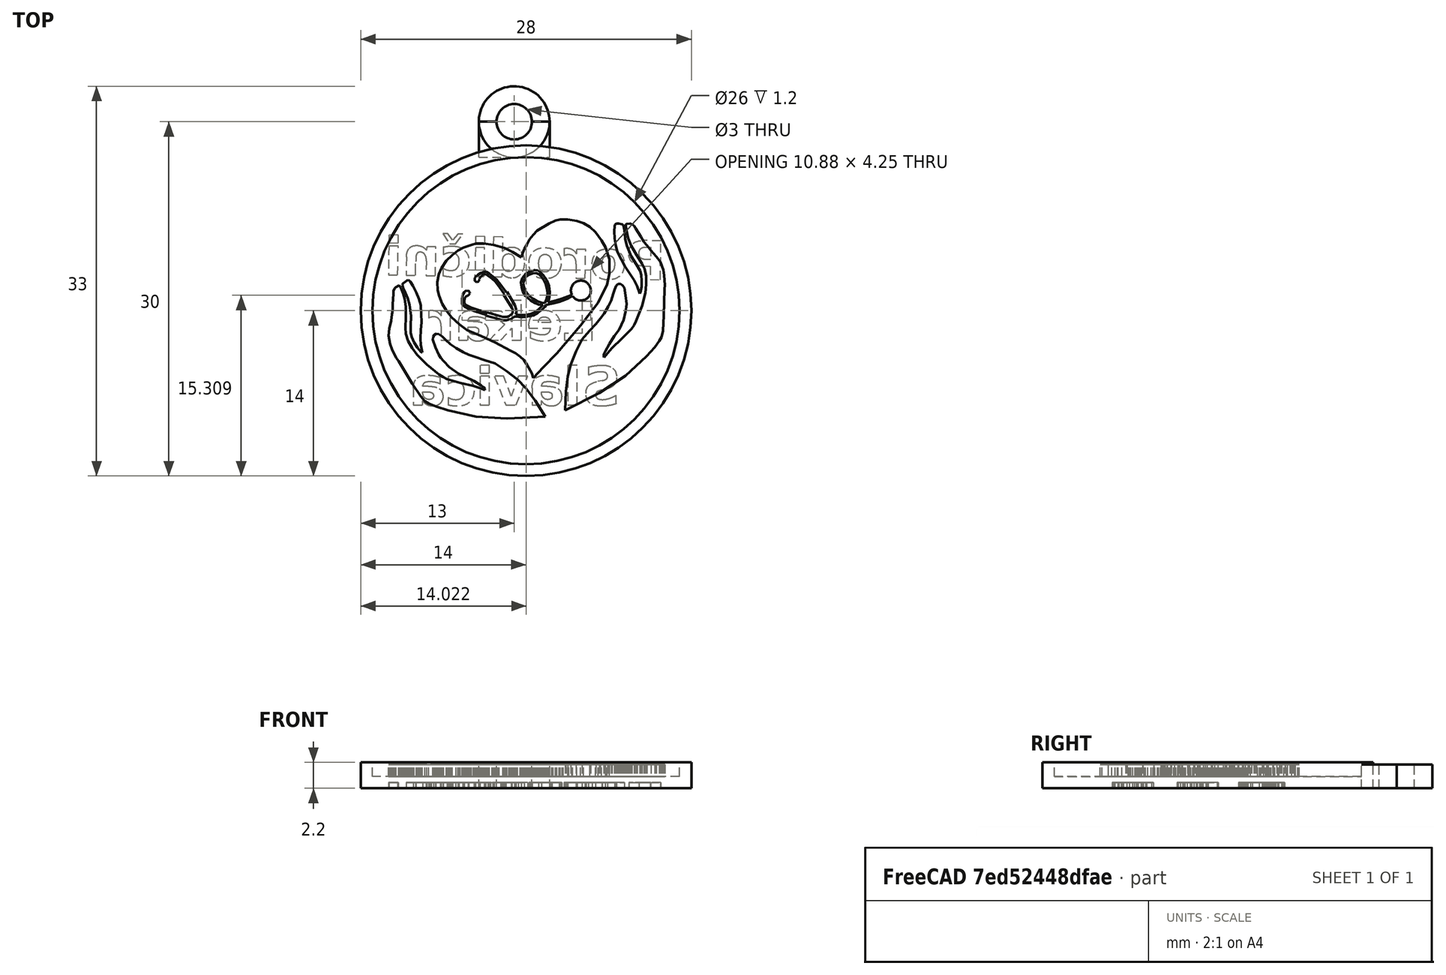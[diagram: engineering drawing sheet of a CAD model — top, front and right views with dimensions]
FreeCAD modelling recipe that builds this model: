
FCSTD DOCUMENT  (FreeCAD 0.19R)
Label: PLS_logo
License: All rights reserved
LicenseURL: http://en.wikipedia.org/wiki/All_rights_reserved
objects: Part::Extrusion×7, Part::Cut×7, Sketcher::SketchObject×4, PartDesign::Body×4, Part::Cylinder×4, Part::Part2DObjectPython×3, Part::Box×1
note: 30 computed .brp shape members not serialized (recipe doc carries the construction recipe); baked Part::Feature solids carry a one-line shape summary decoded from their .brp

FEATURE [Sketcher::SketchObject] Sketch
  MapMode = 5
  Support = -> [XY_Plane]
  sketch-geometry (100):
    g0: LineSegment StartX=-7.99466 StartY=7.65686 StartZ=0 EndX=-8.31629 EndY=7.67321 EndZ=0
    g1: LineSegment StartX=-8.31629 StartY=7.67321 StartZ=0 EndX=-8.46348 EndY=7.62415 EndZ=0
    g2: LineSegment StartX=-8.46348 StartY=7.62415 StartZ=0 EndX=-8.64882 EndY=7.49332 EndZ=0
    g3: LineSegment StartX=-8.64882 StartY=7.49332 StartZ=0 EndX=-8.78511 EndY=7.26436 EndZ=0
    g4: LineSegment StartX=-8.78511 StartY=7.26436 StartZ=0 EndX=-9.23757 EndY=6.56114 EndZ=0
    g5: LineSegment StartX=-9.23757 StartY=6.56114 StartZ=0 EndX=-9.49378 EndY=6.12503 EndZ=0
    g6: LineSegment StartX=-9.49378 StartY=6.12503 StartZ=0 EndX=-9.72819 EndY=5.84156 EndZ=0
    g7: LineSegment StartX=-9.72819 StartY=5.84156 StartZ=0 EndX=-10.0771 EndY=5.40545 EndZ=0
    g8: LineSegment StartX=-10.0771 StartY=5.40545 StartZ=0 EndX=-10.5241 EndY=4.89848 EndZ=0
    g9: LineSegment StartX=-10.5241 StartY=4.89848 StartZ=0 EndX=-10.8784 EndY=4.42966 EndZ=0
    g10: LineSegment StartX=-10.8784 StartY=4.42966 StartZ=0 EndX=-11.1183 EndY=3.7537 EndZ=0
    g11: LineSegment StartX=-11.1183 StartY=3.7537 StartZ=0 EndX=-11.2099 EndY=3.2849 EndZ=0
    g12: LineSegment StartX=-11.2099 StartY=3.2849 StartZ=0 EndX=-11.2683 EndY=2.47003 EndZ=0
    g13: LineSegment StartX=-11.2683 StartY=2.47003 StartZ=0 EndX=-11.2318 EndY=2.13385 EndZ=0
    g14: LineSegment StartX=-11.2318 StartY=2.13385 StartZ=0 EndX=-11.1697 EndY=-0.093535 EndZ=0
    g15: LineSegment StartX=-11.1697 StartY=-0.093535 StartZ=0 EndX=-11.099 EndY=-1.41517 EndZ=0
    g16: LineSegment StartX=-11.099 StartY=-1.41517 StartZ=0 EndX=-10.9851 EndY=-1.92752 EndZ=0
    g17: LineSegment StartX=-10.9851 StartY=-1.92752 StartZ=0 EndX=-10.7981 EndY=-2.25282 EndZ=0
    g18: LineSegment StartX=-10.7981 StartY=-2.25282 StartZ=0 EndX=-10.4077 EndY=-2.78956 EndZ=0
    g19: LineSegment StartX=-10.4077 StartY=-2.78956 StartZ=0 EndX=-9.69294 EndY=-3.55814 EndZ=0
    g20: LineSegment StartX=-9.69294 StartY=-3.55814 StartZ=0 EndX=-7.92061 EndY=-5.20964 EndZ=0
    g21: LineSegment StartX=-7.92061 StartY=-5.20964 StartZ=0 EndX=-5.70519 EndY=-6.65973 EndZ=0
    g22: LineSegment StartX=-5.70519 StartY=-6.65973 StartZ=0 EndX=-2.80501 EndY=-8.1501 EndZ=0
    g23: LineSegment StartX=-2.80501 StartY=-8.1501 StartZ=0 EndX=-2.88557 EndY=-6.53889 EndZ=0
    g24: LineSegment StartX=-2.88557 StartY=-6.53889 StartZ=0 EndX=-3.04596 EndY=-5.2378 EndZ=0
    g25: LineSegment StartX=-3.04596 StartY=-5.2378 StartZ=0 EndX=-3.28765 EndY=-4.27108 EndZ=0
    g26: LineSegment StartX=-3.28765 StartY=-4.27108 StartZ=0 EndX=-3.73073 EndY=-3.14323 EndZ=0
    g27: LineSegment StartX=-3.73073 StartY=-3.14323 StartZ=0 EndX=-4.25437 EndY=-2.13622 EndZ=0
    g28: LineSegment StartX=-4.25437 StartY=-2.13622 StartZ=0 EndX=-4.89343 EndY=-1.4123 EndZ=0
    g29: LineSegment StartX=-4.89343 StartY=-1.4123 StartZ=0 EndX=-5.42724 EndY=-0.829955 EndZ=0
    g30: LineSegment StartX=-5.42724 StartY=-0.829955 StartZ=0 EndX=-5.80334 EndY=-0.368932 EndZ=0
    g31: LineSegment StartX=-5.80334 StartY=-0.368932 StartZ=0 EndX=-6.11862 EndY=0.058717 EndZ=0
    g32: LineSegment StartX=-6.11862 StartY=0.058717 StartZ=0 EndX=-6.47672 EndY=0.661651 EndZ=0
    g33: LineSegment StartX=-6.47672 StartY=0.661651 StartZ=0 EndX=-6.71059 EndY=1.16227 EndZ=0
    g34: LineSegment StartX=-6.71059 StartY=1.16227 StartZ=0 EndX=-6.86944 EndY=1.70125 EndZ=0
    g35: LineSegment StartX=-6.86944 StartY=1.70125 StartZ=0 EndX=-6.99076 EndY=2.10161 EndZ=0
    g36: LineSegment StartX=-6.99076 StartY=2.10161 StartZ=0 EndX=-7.14848 EndY=2.40492 EndZ=0
    g37: LineSegment StartX=-7.14848 StartY=2.40492 StartZ=0 EndX=-7.30619 EndY=2.5505 EndZ=0
    g38: LineSegment StartX=-7.30619 StartY=2.5505 StartZ=0 EndX=-7.51244 EndY=2.5505 EndZ=0
    g39: LineSegment StartX=-7.51244 StartY=2.5505 StartZ=0 EndX=-7.67016 EndY=2.44131 EndZ=0
    g40: LineSegment StartX=-7.67016 StartY=2.44131 StartZ=0 EndX=-7.82788 EndY=2.2472 EndZ=0
    g41: LineSegment StartX=-7.82788 StartY=2.2472 StartZ=0 EndX=-7.93707 EndY=1.59206 EndZ=0
    g42: LineSegment StartX=-7.93707 StartY=1.59206 StartZ=0 EndX=-8.00986 EndY=0.87626 EndZ=0
    g43: LineSegment StartX=-8.00986 StartY=0.87626 StartZ=0 EndX=-7.99773 EndY=0.585087 EndZ=0
    g44: LineSegment StartX=-7.99773 StartY=0.585087 StartZ=0 EndX=-7.92494 EndY=0.221122 EndZ=0
    g45: LineSegment StartX=-7.92494 StartY=0.221122 StartZ=0 EndX=-7.75509 EndY=-0.470414 EndZ=0
    g46: LineSegment StartX=-7.75509 StartY=-0.470414 StartZ=0 EndX=-7.37899 EndY=-1.2954 EndZ=0
    g47: LineSegment StartX=-7.37899 StartY=-1.2954 StartZ=0 EndX=-6.97863 EndY=-1.85348 EndZ=0
    g48: LineSegment StartX=-6.97863 StartY=-1.85348 StartZ=0 EndX=-6.554 EndY=-2.52075 EndZ=0
    g49: LineSegment StartX=-6.554 StartY=-2.52075 StartZ=0 EndX=-6.20216 EndY=-3.16376 EndZ=0
    g50: LineSegment StartX=-6.20216 StartY=-3.16376 StartZ=0 EndX=-6.09298 EndY=-3.41854 EndZ=0
    g51: LineSegment StartX=-6.09298 StartY=-3.41854 StartZ=0 EndX=-6.09298 EndY=-3.57626 EndZ=0
    g52: LineSegment StartX=-6.09298 StartY=-3.57626 StartZ=0 EndX=-6.12937 EndY=-3.66118 EndZ=0
    g53: LineSegment StartX=-6.12937 StartY=-3.66118 StartZ=0 EndX=-6.39628 EndY=-3.32148 EndZ=0
    g54: LineSegment StartX=-6.39628 StartY=-3.32148 StartZ=0 EndX=-6.79664 EndY=-2.84832 EndZ=0
    g55: LineSegment StartX=-6.79664 StartY=-2.84832 StartZ=0 EndX=-7.62163 EndY=-2.07186 EndZ=0
    g56: LineSegment StartX=-7.62163 StartY=-2.07186 StartZ=0 EndX=-8.43449 EndY=-1.24687 EndZ=0
    g57: LineSegment StartX=-8.43449 StartY=-1.24687 StartZ=0 EndX=-8.65287 EndY=-0.919304 EndZ=0
    g58: LineSegment StartX=-8.65287 StartY=-0.919304 StartZ=0 EndX=-8.81059 EndY=-0.579603 EndZ=0
    g59: LineSegment StartX=-8.81059 StartY=-0.579603 StartZ=0 EndX=-9.31856 EndY=0.683537 EndZ=0
    g60: LineSegment StartX=-9.31856 StartY=0.683537 StartZ=0 EndX=-9.60815 EndY=1.80568 EndZ=0
    g61: LineSegment StartX=-9.60815 StartY=1.80568 StartZ=0 EndX=-9.68054 EndY=2.52965 EndZ=0
    g62: LineSegment StartX=-9.68054 StartY=2.52965 StartZ=0 EndX=-9.68054 EndY=3.21741 EndZ=0
    g63: LineSegment StartX=-9.68054 StartY=3.21741 StartZ=0 EndX=-9.55385 EndY=3.83278 EndZ=0
    g64: LineSegment StartX=-9.55385 StartY=3.83278 StartZ=0 EndX=-9.31856 EndY=4.28526 EndZ=0
    g65: LineSegment StartX=-9.31856 StartY=4.28526 StartZ=0 EndX=-8.83633 EndY=5.03517 EndZ=0
    g66: LineSegment StartX=-8.83633 StartY=5.03517 StartZ=0 EndX=-8.40195 EndY=5.81343 EndZ=0
    g67: LineSegment StartX=-8.40195 StartY=5.81343 StartZ=0 EndX=-8.14856 EndY=6.4469 EndZ=0
    g68: LineSegment StartX=-8.14856 StartY=6.4469 StartZ=0 EndX=-8.03997 EndY=6.88128 EndZ=0
    g69: LineSegment StartX=-8.03997 StartY=6.88128 StartZ=0 EndX=-7.96757 EndY=7.38806 EndZ=0
    g70: LineSegment StartX=-7.96757 StartY=7.38806 StartZ=0 EndX=-7.96757 EndY=7.60525 EndZ=0
    g71: LineSegment StartX=-7.96757 StartY=7.60525 StartZ=0 EndX=-7.99466 EndY=7.65686 EndZ=0
    g72: LineSegment StartX=-7.37277 StartY=7.68163 StartZ=0 EndX=-7.63261 EndY=7.62489 EndZ=0
    g73: LineSegment StartX=-7.63261 StartY=7.62489 StartZ=0 EndX=-7.7302 EndY=7.55983 EndZ=0
    g74: LineSegment StartX=-7.7302 StartY=7.55983 StartZ=0 EndX=-7.79526 EndY=7.30773 EndZ=0
    g75: LineSegment StartX=-7.79526 StartY=7.30773 StartZ=0 EndX=-7.86032 EndY=6.83604 EndZ=0
    g76: LineSegment StartX=-7.86032 StartY=6.83604 StartZ=0 EndX=-7.89285 EndY=6.37249 EndZ=0
    g77: LineSegment StartX=-7.89285 StartY=6.37249 StartZ=0 EndX=-8.04736 EndY=5.78695 EndZ=0
    g78: LineSegment StartX=-8.04736 StartY=5.78695 StartZ=0 EndX=-8.41333 EndY=4.91677 EndZ=0
    g79: LineSegment StartX=-8.41333 StartY=4.91677 StartZ=0 EndX=-8.86062 EndY=4.20925 EndZ=0
    g80: LineSegment StartX=-8.86062 StartY=4.20925 StartZ=0 EndX=-9.15339 EndY=3.68877 EndZ=0
    g81: LineSegment StartX=-9.15339 StartY=3.68877 StartZ=0 EndX=-9.25098 EndY=3.32281 EndZ=0
    g82: LineSegment StartX=-9.25098 StartY=3.32281 StartZ=0 EndX=-9.3079 EndY=2.83486 EndZ=0
    g83: LineSegment StartX=-9.3079 StartY=2.83486 StartZ=0 EndX=-9.2835 EndY=2.33878 EndZ=0
    g84: LineSegment StartX=-9.2835 StartY=2.33878 StartZ=0 EndX=-9.21031 EndY=1.87522 EndZ=0
    g85: LineSegment StartX=-9.21031 StartY=1.87522 StartZ=0 EndX=-9.12899 EndY=1.7451 EndZ=0
    g86: LineSegment StartX=-9.12899 StartY=1.7451 StartZ=0 EndX=-8.91754 EndY=2.3713 EndZ=0
    g87: LineSegment StartX=-8.91754 StartY=2.3713 StartZ=0 EndX=-8.64917 EndY=2.88365 EndZ=0
    g88: LineSegment StartX=-8.64917 StartY=2.88365 StartZ=0 EndX=-8.28321 EndY=3.46919 EndZ=0
    g89: LineSegment StartX=-8.28321 StartY=3.46919 StartZ=0 EndX=-7.89285 EndY=4.0222 EndZ=0
    g90: LineSegment StartX=-7.89285 StartY=4.0222 StartZ=0 EndX=-7.57568 EndY=4.64027 EndZ=0
    g91: LineSegment StartX=-7.57568 StartY=4.64027 StartZ=0 EndX=-7.24225 EndY=5.29087 EndZ=0
    g92: LineSegment StartX=-7.24225 StartY=5.29087 StartZ=0 EndX=-7.104 EndY=5.82761 EndZ=0
    g93: LineSegment StartX=-7.104 StartY=5.82761 StartZ=0 EndX=-7.01454 EndY=6.41315 EndZ=0
    g94: LineSegment StartX=-7.01454 StartY=6.41315 StartZ=0 EndX=-6.99014 EndY=7.03935 EndZ=0
    g95: LineSegment StartX=-6.99014 StartY=7.03935 StartZ=0 EndX=-7.01454 EndY=7.44598 EndZ=0
    g96: LineSegment StartX=-7.01454 StartY=7.44598 StartZ=0 EndX=-7.0308 EndY=7.59236 EndZ=0
    g97: LineSegment StartX=-7.0308 StartY=7.59236 StartZ=0 EndX=-7.104 EndY=7.64929 EndZ=0
    g98: LineSegment StartX=-7.104 StartY=7.64929 StartZ=0 EndX=-7.20972 EndY=7.67369 EndZ=0
    g99: LineSegment StartX=-7.20972 StartY=7.67369 StartZ=0 EndX=-7.37277 EndY=7.68163 EndZ=0
  constraints (98):
    c: Coincident(g0,g1)
    c: Coincident(g1,g2)
    c: Coincident(g2,g3)
    c: Coincident(g3,g4)
    c: Coincident(g4,g5)
    c: Coincident(g5,g6)
    c: Coincident(g6,g7)
    c: Coincident(g7,g8)
    c: Coincident(g8,g9)
    c: Coincident(g9,g10)
    c: Coincident(g10,g11)
    c: Coincident(g11,g12)
    c: Coincident(g12,g13)
    c: Coincident(g13,g14)
    c: Coincident(g14,g15)
    c: Coincident(g15,g16)
    c: Coincident(g16,g17)
    c: Coincident(g17,g18)
    c: Coincident(g18,g19)
    c: Coincident(g19,g20)
    c: Coincident(g20,g21)
    c: Coincident(g21,g22)
    c: Coincident(g22,g23)
    c: Coincident(g23,g24)
    c: Coincident(g24,g25)
    c: Coincident(g25,g26)
    c: Coincident(g26,g27)
    c: Coincident(g27,g28)
    c: Coincident(g28,g29)
    c: Coincident(g29,g30)
    c: Coincident(g31,g32)
    c: Coincident(g32,g33)
    c: Coincident(g33,g34)
    c: Coincident(g34,g35)
    c: Coincident(g35,g36)
    c: Coincident(g36,g37)
    c: Coincident(g37,g38)
    c: Coincident(g38,g39)
    c: Coincident(g39,g40)
    c: Coincident(g40,g41)
    c: Coincident(g41,g42)
    c: Coincident(g42,g43)
    c: Coincident(g43,g44)
    c: Coincident(g44,g45)
    c: Coincident(g45,g46)
    c: Coincident(g46,g47)
    c: Coincident(g47,g48)
    c: Coincident(g48,g49)
    c: Coincident(g49,g50)
    c: Coincident(g50,g51)
    c: Coincident(g51,g52)
    c: Coincident(g52,g53)
    c: Coincident(g53,g54)
    c: Coincident(g54,g55)
    c: Coincident(g55,g56)
    c: Coincident(g56,g57)
    c: Coincident(g57,g58)
    c: Coincident(g58,g59)
    c: Coincident(g59,g60)
    c: Coincident(g60,g61)
    c: Coincident(g61,g62)
    c: Coincident(g62,g63)
    c: Coincident(g63,g64)
    c: Coincident(g64,g65)
    c: Coincident(g65,g66)
    c: Coincident(g66,g67)
    c: Coincident(g67,g68)
    c: Coincident(g68,g69)
    c: Coincident(g69,g70)
    c: Coincident(g0,g71)
    c: Coincident(g72,g73)
    c: Coincident(g73,g74)
    c: Coincident(g74,g75)
    c: Coincident(g75,g76)
    c: Coincident(g76,g77)
    c: Coincident(g77,g78)
    c: Coincident(g78,g79)
    c: Coincident(g79,g80)
    c: Coincident(g80,g81)
    c: Coincident(g81,g82)
    c: Coincident(g82,g83)
    c: Coincident(g83,g84)
    c: Coincident(g84,g85)
    c: Coincident(g85,g86)
    c: Coincident(g86,g87)
    c: Coincident(g87,g88)
    c: Coincident(g88,g89)
    c: Coincident(g89,g90)
    c: Coincident(g90,g91)
    c: Coincident(g91,g92)
    c: Coincident(g92,g93)
    c: Coincident(g93,g94)
    c: Coincident(g94,g95)
    c: Coincident(g95,g96)
    c: Coincident(g96,g97)
    c: Coincident(g97,g98)
    c: Coincident(g98,g99)
    c: Coincident(g99,g72)
FEATURE [PartDesign::Body] Body
  Group = -> [Sketch]
  Origin = -> Origin
FEATURE [Part::Extrusion] Extrude
  Base = -> Sketch
  Dir = (0,0,1)
  DirMode = 2
  FaceMakerClass = Part::FaceMakerBullseye
  LengthFwd = 1
  LengthRev = 0
  Placement = pos=(1,19.5,1) rot=(0,0,1;0.523599rad)
  Solid = true
  Symmetric = false
FEATURE [Sketcher::SketchObject] Sketch001
  MapMode = 5
  Support = -> [XY_Plane001]
  sketch-geometry (100):
    g0: LineSegment StartX=-7.99466 StartY=7.65686 StartZ=0 EndX=-8.31629 EndY=7.67321 EndZ=0
    g1: LineSegment StartX=-8.31629 StartY=7.67321 StartZ=0 EndX=-8.46348 EndY=7.62415 EndZ=0
    g2: LineSegment StartX=-8.46348 StartY=7.62415 StartZ=0 EndX=-8.64882 EndY=7.49332 EndZ=0
    g3: LineSegment StartX=-8.64882 StartY=7.49332 StartZ=0 EndX=-8.78511 EndY=7.26436 EndZ=0
    g4: LineSegment StartX=-8.78511 StartY=7.26436 StartZ=0 EndX=-9.23757 EndY=6.56114 EndZ=0
    g5: LineSegment StartX=-9.23757 StartY=6.56114 StartZ=0 EndX=-9.49378 EndY=6.12503 EndZ=0
    g6: LineSegment StartX=-9.49378 StartY=6.12503 StartZ=0 EndX=-9.72819 EndY=5.84156 EndZ=0
    g7: LineSegment StartX=-9.72819 StartY=5.84156 StartZ=0 EndX=-10.0771 EndY=5.40545 EndZ=0
    g8: LineSegment StartX=-10.0771 StartY=5.40545 StartZ=0 EndX=-10.5241 EndY=4.89848 EndZ=0
    g9: LineSegment StartX=-10.5241 StartY=4.89848 StartZ=0 EndX=-10.8784 EndY=4.42966 EndZ=0
    g10: LineSegment StartX=-10.8784 StartY=4.42966 StartZ=0 EndX=-11.1183 EndY=3.7537 EndZ=0
    g11: LineSegment StartX=-11.1183 StartY=3.7537 StartZ=0 EndX=-11.2099 EndY=3.2849 EndZ=0
    g12: LineSegment StartX=-11.2099 StartY=3.2849 StartZ=0 EndX=-11.2683 EndY=2.47003 EndZ=0
    g13: LineSegment StartX=-11.2683 StartY=2.47003 StartZ=0 EndX=-11.2318 EndY=2.13385 EndZ=0
    g14: LineSegment StartX=-11.2318 StartY=2.13385 StartZ=0 EndX=-11.1697 EndY=-0.093535 EndZ=0
    g15: LineSegment StartX=-11.1697 StartY=-0.093535 StartZ=0 EndX=-11.099 EndY=-1.41517 EndZ=0
    g16: LineSegment StartX=-11.099 StartY=-1.41517 StartZ=0 EndX=-10.9851 EndY=-1.92752 EndZ=0
    g17: LineSegment StartX=-10.9851 StartY=-1.92752 StartZ=0 EndX=-10.7981 EndY=-2.25282 EndZ=0
    g18: LineSegment StartX=-10.7981 StartY=-2.25282 StartZ=0 EndX=-10.4077 EndY=-2.78956 EndZ=0
    g19: LineSegment StartX=-10.4077 StartY=-2.78956 StartZ=0 EndX=-9.69294 EndY=-3.55814 EndZ=0
    g20: LineSegment StartX=-9.69294 StartY=-3.55814 StartZ=0 EndX=-7.92061 EndY=-5.20964 EndZ=0
    g21: LineSegment StartX=-7.92061 StartY=-5.20964 StartZ=0 EndX=-5.70519 EndY=-6.65973 EndZ=0
    g22: LineSegment StartX=-5.70519 StartY=-6.65973 StartZ=0 EndX=-2.80501 EndY=-8.1501 EndZ=0
    g23: LineSegment StartX=-2.80501 StartY=-8.1501 StartZ=0 EndX=-2.88557 EndY=-6.53889 EndZ=0
    g24: LineSegment StartX=-2.88557 StartY=-6.53889 StartZ=0 EndX=-3.04596 EndY=-5.2378 EndZ=0
    g25: LineSegment StartX=-3.04596 StartY=-5.2378 StartZ=0 EndX=-3.28765 EndY=-4.27108 EndZ=0
    g26: LineSegment StartX=-3.28765 StartY=-4.27108 StartZ=0 EndX=-3.73073 EndY=-3.14323 EndZ=0
    g27: LineSegment StartX=-3.73073 StartY=-3.14323 StartZ=0 EndX=-4.25437 EndY=-2.13622 EndZ=0
    g28: LineSegment StartX=-4.25437 StartY=-2.13622 StartZ=0 EndX=-4.89343 EndY=-1.4123 EndZ=0
    g29: LineSegment StartX=-4.89343 StartY=-1.4123 StartZ=0 EndX=-5.42724 EndY=-0.829955 EndZ=0
    g30: LineSegment StartX=-5.42724 StartY=-0.829955 StartZ=0 EndX=-5.80334 EndY=-0.368932 EndZ=0
    g31: LineSegment StartX=-5.80334 StartY=-0.368932 StartZ=0 EndX=-6.11862 EndY=0.058717 EndZ=0
    g32: LineSegment StartX=-6.11862 StartY=0.058717 StartZ=0 EndX=-6.47672 EndY=0.661651 EndZ=0
    g33: LineSegment StartX=-6.47672 StartY=0.661651 StartZ=0 EndX=-6.71059 EndY=1.16227 EndZ=0
    g34: LineSegment StartX=-6.71059 StartY=1.16227 StartZ=0 EndX=-6.86944 EndY=1.70125 EndZ=0
    g35: LineSegment StartX=-6.86944 StartY=1.70125 StartZ=0 EndX=-6.99076 EndY=2.10161 EndZ=0
    g36: LineSegment StartX=-6.99076 StartY=2.10161 StartZ=0 EndX=-7.14848 EndY=2.40492 EndZ=0
    g37: LineSegment StartX=-7.14848 StartY=2.40492 StartZ=0 EndX=-7.30619 EndY=2.5505 EndZ=0
    g38: LineSegment StartX=-7.30619 StartY=2.5505 StartZ=0 EndX=-7.51244 EndY=2.5505 EndZ=0
    g39: LineSegment StartX=-7.51244 StartY=2.5505 StartZ=0 EndX=-7.67016 EndY=2.44131 EndZ=0
    g40: LineSegment StartX=-7.67016 StartY=2.44131 StartZ=0 EndX=-7.82788 EndY=2.2472 EndZ=0
    g41: LineSegment StartX=-7.82788 StartY=2.2472 StartZ=0 EndX=-7.93707 EndY=1.59206 EndZ=0
    g42: LineSegment StartX=-7.93707 StartY=1.59206 StartZ=0 EndX=-8.00986 EndY=0.87626 EndZ=0
    g43: LineSegment StartX=-8.00986 StartY=0.87626 StartZ=0 EndX=-7.99773 EndY=0.585087 EndZ=0
    g44: LineSegment StartX=-7.99773 StartY=0.585087 StartZ=0 EndX=-7.92494 EndY=0.221122 EndZ=0
    g45: LineSegment StartX=-7.92494 StartY=0.221122 StartZ=0 EndX=-7.75509 EndY=-0.470414 EndZ=0
    g46: LineSegment StartX=-7.75509 StartY=-0.470414 StartZ=0 EndX=-7.37899 EndY=-1.2954 EndZ=0
    g47: LineSegment StartX=-7.37899 StartY=-1.2954 StartZ=0 EndX=-6.97863 EndY=-1.85348 EndZ=0
    g48: LineSegment StartX=-6.97863 StartY=-1.85348 StartZ=0 EndX=-6.554 EndY=-2.52075 EndZ=0
    g49: LineSegment StartX=-6.554 StartY=-2.52075 StartZ=0 EndX=-6.20216 EndY=-3.16376 EndZ=0
    g50: LineSegment StartX=-6.20216 StartY=-3.16376 StartZ=0 EndX=-6.09298 EndY=-3.41854 EndZ=0
    g51: LineSegment StartX=-6.09298 StartY=-3.41854 StartZ=0 EndX=-6.09298 EndY=-3.57626 EndZ=0
    g52: LineSegment StartX=-6.09298 StartY=-3.57626 StartZ=0 EndX=-6.12937 EndY=-3.66118 EndZ=0
    g53: LineSegment StartX=-6.12937 StartY=-3.66118 StartZ=0 EndX=-6.39628 EndY=-3.32148 EndZ=0
    g54: LineSegment StartX=-6.39628 StartY=-3.32148 StartZ=0 EndX=-6.79664 EndY=-2.84832 EndZ=0
    g55: LineSegment StartX=-6.79664 StartY=-2.84832 StartZ=0 EndX=-7.62163 EndY=-2.07186 EndZ=0
    g56: LineSegment StartX=-7.62163 StartY=-2.07186 StartZ=0 EndX=-8.43449 EndY=-1.24687 EndZ=0
    g57: LineSegment StartX=-8.43449 StartY=-1.24687 StartZ=0 EndX=-8.65287 EndY=-0.919304 EndZ=0
    g58: LineSegment StartX=-8.65287 StartY=-0.919304 StartZ=0 EndX=-8.81059 EndY=-0.579603 EndZ=0
    g59: LineSegment StartX=-8.81059 StartY=-0.579603 StartZ=0 EndX=-9.31856 EndY=0.683537 EndZ=0
    g60: LineSegment StartX=-9.31856 StartY=0.683537 StartZ=0 EndX=-9.60815 EndY=1.80568 EndZ=0
    g61: LineSegment StartX=-9.60815 StartY=1.80568 StartZ=0 EndX=-9.68054 EndY=2.52965 EndZ=0
    g62: LineSegment StartX=-9.68054 StartY=2.52965 StartZ=0 EndX=-9.68054 EndY=3.21741 EndZ=0
    g63: LineSegment StartX=-9.68054 StartY=3.21741 StartZ=0 EndX=-9.55385 EndY=3.83278 EndZ=0
    g64: LineSegment StartX=-9.55385 StartY=3.83278 StartZ=0 EndX=-9.31856 EndY=4.28526 EndZ=0
    g65: LineSegment StartX=-9.31856 StartY=4.28526 StartZ=0 EndX=-8.83633 EndY=5.03517 EndZ=0
    g66: LineSegment StartX=-8.83633 StartY=5.03517 StartZ=0 EndX=-8.40195 EndY=5.81343 EndZ=0
    g67: LineSegment StartX=-8.40195 StartY=5.81343 StartZ=0 EndX=-8.14856 EndY=6.4469 EndZ=0
    g68: LineSegment StartX=-8.14856 StartY=6.4469 StartZ=0 EndX=-8.03997 EndY=6.88128 EndZ=0
    g69: LineSegment StartX=-8.03997 StartY=6.88128 StartZ=0 EndX=-7.96757 EndY=7.38806 EndZ=0
    g70: LineSegment StartX=-7.96757 StartY=7.38806 StartZ=0 EndX=-7.96757 EndY=7.60525 EndZ=0
    g71: LineSegment StartX=-7.96757 StartY=7.60525 StartZ=0 EndX=-7.99466 EndY=7.65686 EndZ=0
    g72: LineSegment StartX=-7.37277 StartY=7.68163 StartZ=0 EndX=-7.63261 EndY=7.62489 EndZ=0
    g73: LineSegment StartX=-7.63261 StartY=7.62489 StartZ=0 EndX=-7.7302 EndY=7.55983 EndZ=0
    g74: LineSegment StartX=-7.7302 StartY=7.55983 StartZ=0 EndX=-7.79526 EndY=7.30773 EndZ=0
    g75: LineSegment StartX=-7.79526 StartY=7.30773 StartZ=0 EndX=-7.86032 EndY=6.83604 EndZ=0
    g76: LineSegment StartX=-7.86032 StartY=6.83604 StartZ=0 EndX=-7.89285 EndY=6.37249 EndZ=0
    g77: LineSegment StartX=-7.89285 StartY=6.37249 StartZ=0 EndX=-8.04736 EndY=5.78695 EndZ=0
    g78: LineSegment StartX=-8.04736 StartY=5.78695 StartZ=0 EndX=-8.41333 EndY=4.91677 EndZ=0
    g79: LineSegment StartX=-8.41333 StartY=4.91677 StartZ=0 EndX=-8.86062 EndY=4.20925 EndZ=0
    g80: LineSegment StartX=-8.86062 StartY=4.20925 StartZ=0 EndX=-9.15339 EndY=3.68877 EndZ=0
    g81: LineSegment StartX=-9.15339 StartY=3.68877 StartZ=0 EndX=-9.25098 EndY=3.32281 EndZ=0
    g82: LineSegment StartX=-9.25098 StartY=3.32281 StartZ=0 EndX=-9.3079 EndY=2.83486 EndZ=0
    g83: LineSegment StartX=-9.3079 StartY=2.83486 StartZ=0 EndX=-9.2835 EndY=2.33878 EndZ=0
    g84: LineSegment StartX=-9.2835 StartY=2.33878 StartZ=0 EndX=-9.21031 EndY=1.87522 EndZ=0
    g85: LineSegment StartX=-9.21031 StartY=1.87522 StartZ=0 EndX=-9.12899 EndY=1.7451 EndZ=0
    g86: LineSegment StartX=-9.12899 StartY=1.7451 StartZ=0 EndX=-8.91754 EndY=2.3713 EndZ=0
    g87: LineSegment StartX=-8.91754 StartY=2.3713 StartZ=0 EndX=-8.64917 EndY=2.88365 EndZ=0
    g88: LineSegment StartX=-8.64917 StartY=2.88365 StartZ=0 EndX=-8.28321 EndY=3.46919 EndZ=0
    g89: LineSegment StartX=-8.28321 StartY=3.46919 StartZ=0 EndX=-7.89285 EndY=4.0222 EndZ=0
    g90: LineSegment StartX=-7.89285 StartY=4.0222 StartZ=0 EndX=-7.57568 EndY=4.64027 EndZ=0
    g91: LineSegment StartX=-7.57568 StartY=4.64027 StartZ=0 EndX=-7.24225 EndY=5.29087 EndZ=0
    g92: LineSegment StartX=-7.24225 StartY=5.29087 StartZ=0 EndX=-7.104 EndY=5.82761 EndZ=0
    g93: LineSegment StartX=-7.104 StartY=5.82761 StartZ=0 EndX=-7.01454 EndY=6.41315 EndZ=0
    g94: LineSegment StartX=-7.01454 StartY=6.41315 StartZ=0 EndX=-6.99014 EndY=7.03935 EndZ=0
    g95: LineSegment StartX=-6.99014 StartY=7.03935 StartZ=0 EndX=-7.01454 EndY=7.44598 EndZ=0
    g96: LineSegment StartX=-7.01454 StartY=7.44598 StartZ=0 EndX=-7.0308 EndY=7.59236 EndZ=0
    g97: LineSegment StartX=-7.0308 StartY=7.59236 StartZ=0 EndX=-7.104 EndY=7.64929 EndZ=0
    g98: LineSegment StartX=-7.104 StartY=7.64929 StartZ=0 EndX=-7.20972 EndY=7.67369 EndZ=0
    g99: LineSegment StartX=-7.20972 StartY=7.67369 StartZ=0 EndX=-7.37277 EndY=7.68163 EndZ=0
  constraints (98):
    c: Coincident(g0,g1)
    c: Coincident(g1,g2)
    c: Coincident(g2,g3)
    c: Coincident(g3,g4)
    c: Coincident(g4,g5)
    c: Coincident(g5,g6)
    c: Coincident(g6,g7)
    c: Coincident(g7,g8)
    c: Coincident(g8,g9)
    c: Coincident(g9,g10)
    c: Coincident(g10,g11)
    c: Coincident(g11,g12)
    c: Coincident(g12,g13)
    c: Coincident(g13,g14)
    c: Coincident(g14,g15)
    c: Coincident(g15,g16)
    c: Coincident(g16,g17)
    c: Coincident(g17,g18)
    c: Coincident(g18,g19)
    c: Coincident(g19,g20)
    c: Coincident(g20,g21)
    c: Coincident(g21,g22)
    c: Coincident(g22,g23)
    c: Coincident(g23,g24)
    c: Coincident(g24,g25)
    c: Coincident(g25,g26)
    c: Coincident(g26,g27)
    c: Coincident(g27,g28)
    c: Coincident(g28,g29)
    c: Coincident(g29,g30)
    c: Coincident(g31,g32)
    c: Coincident(g32,g33)
    c: Coincident(g33,g34)
    c: Coincident(g34,g35)
    c: Coincident(g35,g36)
    c: Coincident(g36,g37)
    c: Coincident(g37,g38)
    c: Coincident(g38,g39)
    c: Coincident(g39,g40)
    c: Coincident(g40,g41)
    c: Coincident(g41,g42)
    c: Coincident(g42,g43)
    c: Coincident(g43,g44)
    c: Coincident(g44,g45)
    c: Coincident(g45,g46)
    c: Coincident(g46,g47)
    c: Coincident(g47,g48)
    c: Coincident(g48,g49)
    c: Coincident(g49,g50)
    c: Coincident(g50,g51)
    c: Coincident(g51,g52)
    c: Coincident(g52,g53)
    c: Coincident(g53,g54)
    c: Coincident(g54,g55)
    c: Coincident(g55,g56)
    c: Coincident(g56,g57)
    c: Coincident(g57,g58)
    c: Coincident(g58,g59)
    c: Coincident(g59,g60)
    c: Coincident(g60,g61)
    c: Coincident(g61,g62)
    c: Coincident(g62,g63)
    c: Coincident(g63,g64)
    c: Coincident(g64,g65)
    c: Coincident(g65,g66)
    c: Coincident(g66,g67)
    c: Coincident(g67,g68)
    c: Coincident(g68,g69)
    c: Coincident(g69,g70)
    c: Coincident(g0,g71)
    c: Coincident(g72,g73)
    c: Coincident(g73,g74)
    c: Coincident(g74,g75)
    c: Coincident(g75,g76)
    c: Coincident(g76,g77)
    c: Coincident(g77,g78)
    c: Coincident(g78,g79)
    c: Coincident(g79,g80)
    c: Coincident(g80,g81)
    c: Coincident(g81,g82)
    c: Coincident(g82,g83)
    c: Coincident(g83,g84)
    c: Coincident(g84,g85)
    c: Coincident(g85,g86)
    c: Coincident(g86,g87)
    c: Coincident(g87,g88)
    c: Coincident(g88,g89)
    c: Coincident(g89,g90)
    c: Coincident(g90,g91)
    c: Coincident(g91,g92)
    c: Coincident(g92,g93)
    c: Coincident(g93,g94)
    c: Coincident(g94,g95)
    c: Coincident(g95,g96)
    c: Coincident(g96,g97)
    c: Coincident(g97,g98)
    c: Coincident(g98,g99)
    c: Coincident(g99,g72)
FEATURE [Sketcher::SketchObject] Sketch002
  MapMode = 5
  Support = -> [XY_Plane002]
  sketch-geometry (53):
    g0: LineSegment StartX=-1.58869 StartY=8.51607 StartZ=0 EndX=-2.26809 EndY=8.62526 EndZ=0
    g1: LineSegment StartX=-2.26809 StartY=8.62526 StartZ=0 EndX=-2.8019 EndY=8.64952 EndZ=0
    g2: LineSegment StartX=-2.8019 StartY=8.64952 StartZ=0 EndX=-3.42064 EndY=8.57673 EndZ=0
    g3: LineSegment StartX=-3.42064 StartY=8.57673 StartZ=0 EndX=-4.10005 EndY=8.40688 EndZ=0
    g4: LineSegment StartX=-4.10005 StartY=8.40688 StartZ=0 EndX=-4.76732 EndY=8.07931 EndZ=0
    g5: LineSegment StartX=-4.76732 StartY=8.07931 StartZ=0 EndX=-5.21621 EndY=7.73961 EndZ=0
    g6: LineSegment StartX=-5.21621 StartY=7.73961 StartZ=0 EndX=-5.65297 EndY=7.21793 EndZ=0
    g7: LineSegment StartX=-5.65297 StartY=7.21793 StartZ=0 EndX=-5.98054 EndY=6.59919 EndZ=0
    g8: LineSegment StartX=-5.98054 StartY=6.59919 StartZ=0 EndX=-6.11399 EndY=6.1139 EndZ=0
    g9: LineSegment StartX=-6.11399 StartY=6.1139 StartZ=0 EndX=-6.23531 EndY=5.41023 EndZ=0
    g10: LineSegment StartX=-6.23531 StartY=5.41023 StartZ=0 EndX=-6.19892 EndY=4.75509 EndZ=0
    g11: LineSegment StartX=-6.19892 StartY=4.75509 StartZ=0 EndX=-6.11399 EndY=4.05143 EndZ=0
    g12: LineSegment StartX=-6.11399 StartY=4.05143 StartZ=0 EndX=-5.82282 EndY=3.19004 EndZ=0
    g13: LineSegment StartX=-5.82282 StartY=3.19004 StartZ=0 EndX=-5.50738 EndY=2.43785 EndZ=0
    g14: LineSegment StartX=-5.50738 StartY=2.43785 StartZ=0 EndX=-4.73092 EndY=1.40661 EndZ=0
    g15: LineSegment StartX=-4.73092 StartY=1.40661 StartZ=0 EndX=-3.98305 EndY=0.340156 EndZ=0
    g16: LineSegment StartX=-3.98305 StartY=0.340156 StartZ=0 EndX=-3.20233 EndY=-0.904109 EndZ=0
    g17: LineSegment StartX=-3.20233 StartY=-0.904109 StartZ=0 EndX=-2.93268 EndY=-1.32413 EndZ=0
    g18: LineSegment StartX=-2.93268 StartY=-1.32413 StartZ=0 EndX=-2.72553 EndY=-1.75479 EndZ=0
    g19: LineSegment StartX=-2.72553 StartY=-1.75479 StartZ=0 EndX=-2.62195 EndY=-2.16364 EndZ=0
    g20: LineSegment StartX=-2.62195 StartY=-2.16364 StartZ=0 EndX=-2.57289 EndY=-2.70332 EndZ=0
    g21: LineSegment StartX=-2.57289 StartY=-2.70332 StartZ=0 EndX=-2.58924 EndY=-3.4556 EndZ=0
    g22: LineSegment StartX=-2.58924 StartY=-3.4556 StartZ=0 EndX=-2.67102 EndY=-3.87536 EndZ=0
    g23: LineSegment StartX=-2.67102 StartY=-3.87536 StartZ=0 EndX=-1.48262 EndY=-3.51557 EndZ=0
    g24: LineSegment StartX=-1.48262 StartY=-3.51557 StartZ=0 EndX=0.092815 EndY=-3.06311 EndZ=0
    g25: LineSegment StartX=0.092815 StartY=-3.06311 StartZ=0 EndX=3.01261 EndY=-2.045 EndZ=0
    g26: LineSegment StartX=3.01261 StartY=-2.045 StartZ=0 EndX=5.275 EndY=-1.10385 EndZ=0
    g27: LineSegment StartX=5.275 StartY=-1.10385 StartZ=0 EndX=6.70483 EndY=-0.144598 EndZ=0
    g28: LineSegment StartX=6.70483 StartY=-0.144598 StartZ=0 EndX=7.33829 EndY=0.561267 EndZ=0
    g29: LineSegment StartX=7.33829 StartY=0.561267 StartZ=0 EndX=7.93557 EndY=1.61102 EndZ=0
    g30: LineSegment StartX=7.93557 StartY=1.61102 StartZ=0 EndX=8.14627 EndY=2.62316 EndZ=0
    g31: LineSegment StartX=8.14627 StartY=2.62316 StartZ=0 EndX=8.13814 EndY=3.32255 EndZ=0
    g32: LineSegment StartX=8.13814 StartY=3.32255 StartZ=0 EndX=8.06495 EndY=4.17646 EndZ=0
    g33: LineSegment StartX=8.06495 StartY=4.17646 StartZ=0 EndX=7.86519 EndY=4.81764 EndZ=0
    g34: LineSegment StartX=7.86519 StartY=4.81764 StartZ=0 EndX=7.57402 EndY=5.35146 EndZ=0
    g35: LineSegment StartX=7.57402 StartY=5.35146 StartZ=0 EndX=7.16153 EndY=5.81248 EndZ=0
    g36: LineSegment StartX=7.16153 StartY=5.81248 StartZ=0 EndX=6.55492 EndY=6.29777 EndZ=0
    g37: LineSegment StartX=6.55492 StartY=6.29777 StartZ=0 EndX=6.01286 EndY=6.59157 EndZ=0
    g38: LineSegment StartX=6.01286 StartY=6.59157 StartZ=0 EndX=5.60624 EndY=6.72982 EndZ=0
    g39: LineSegment StartX=5.60624 StartY=6.72982 StartZ=0 EndX=4.99631 EndY=6.77049 EndZ=0
    g40: LineSegment StartX=4.99631 StartY=6.77049 StartZ=0 EndX=3.83336 EndY=6.76235 EndZ=0
    g41: LineSegment StartX=3.83336 StartY=6.76235 StartZ=0 EndX=3.37795 EndY=6.63223 EndZ=0
    g42: LineSegment StartX=3.37795 StartY=6.63223 StartZ=0 EndX=2.92253 EndY=6.43705 EndZ=0
    g43: LineSegment StartX=2.92253 StartY=6.43705 StartZ=0 EndX=2.48338 EndY=6.17682 EndZ=0
    g44: LineSegment StartX=2.48338 StartY=6.17682 StartZ=0 EndX=2.11741 EndY=5.94097 EndZ=0
    g45: LineSegment StartX=2.11741 StartY=5.94097 StartZ=0 EndX=1.83278 EndY=5.7458 EndZ=0
    g46: LineSegment StartX=1.83278 StartY=5.7458 StartZ=0 EndX=1.54001 EndY=5.47743 EndZ=0
    g47: LineSegment StartX=1.54001 StartY=5.47743 StartZ=0 EndX=1.14965 EndY=6.21748 EndZ=0
    g48: LineSegment StartX=1.14965 StartY=6.21748 StartZ=0 EndX=0.686102 EndY=6.87621 EndZ=0
    g49: LineSegment StartX=0.686102 StartY=6.87621 StartZ=0 EndX=0.04516 EndY=7.55052 EndZ=0
    g50: LineSegment StartX=0.04516 StartY=7.55052 StartZ=0 EndX=-0.646099 EndY=8.0954 EndZ=0
    g51: LineSegment StartX=-0.646099 StartY=8.0954 StartZ=0 EndX=-1.15844 EndY=8.3963 EndZ=0
    g52: LineSegment StartX=-1.15844 StartY=8.3963 StartZ=0 EndX=-1.58869 EndY=8.51607 EndZ=0
  constraints (52):
    c: Coincident(g0,g1)
    c: Coincident(g1,g2)
    c: Coincident(g2,g3)
    c: Coincident(g3,g4)
    c: Coincident(g4,g5)
    c: Coincident(g5,g6)
    c: Coincident(g6,g7)
    c: Coincident(g7,g8)
    c: Coincident(g8,g9)
    c: Coincident(g9,g10)
    c: Coincident(g10,g11)
    c: Coincident(g11,g12)
    c: Coincident(g12,g13)
    c: Coincident(g13,g14)
    c: Coincident(g14,g15)
    c: Coincident(g15,g16)
    c: Coincident(g16,g17)
    c: Coincident(g17,g18)
    c: Coincident(g18,g19)
    c: Coincident(g19,g20)
    c: Coincident(g20,g21)
    c: Coincident(g21,g22)
    c: Coincident(g22,g23)
    c: Coincident(g23,g24)
    c: Coincident(g24,g25)
    c: Coincident(g25,g26)
    c: Coincident(g26,g27)
    c: Coincident(g27,g28)
    c: Coincident(g28,g29)
    c: Coincident(g29,g30)
    c: Coincident(g30,g31)
    c: Coincident(g31,g32)
    c: Coincident(g33,g34)
    c: Coincident(g34,g35)
    c: Coincident(g35,g36)
    c: Coincident(g36,g37)
    c: Coincident(g37,g38)
    c: Coincident(g38,g39)
    c: Coincident(g39,g40)
    c: Coincident(g40,g41)
    c: Coincident(g41,g42)
    c: Coincident(g42,g43)
    c: Coincident(g43,g44)
    c: Coincident(g44,g45)
    c: Coincident(g45,g46)
    c: Coincident(g46,g47)
    c: Coincident(g47,g48)
    c: Coincident(g48,g49)
    c: Coincident(g49,g50)
    c: Coincident(g50,g51)
    c: Coincident(g51,g52)
    c: Coincident(g0,g52)
FEATURE [PartDesign::Body] Body001
  Group = -> [Sketch002]
  Origin = -> Origin001
FEATURE [Part::Extrusion] Extrude002
  Base = -> Sketch002
  Dir = (0,0,1)
  DirMode = 2
  FaceMakerClass = Part::FaceMakerBullseye
  LengthFwd = 1
  LengthRev = 0
  Placement = pos=(2,19,0) rot=(0,0,1;0.523599rad)
  Solid = true
  Symmetric = false
FEATURE [PartDesign::Body] Body002
  Origin = -> Origin002
FEATURE [Sketcher::SketchObject] Sketch003
  MapMode = 5
  Support = -> [XY_Plane004]
  sketch-geometry (147):
    g0: LineSegment StartX=-4.74287 StartY=4.61966 StartZ=0 EndX=-4.55753 EndY=4.91949 EndZ=0
    g1: LineSegment StartX=-4.55753 StartY=4.91949 StartZ=0 EndX=-4.4267 EndY=5.12119 EndZ=0
    g2: LineSegment StartX=-4.4267 StartY=5.12119 StartZ=0 EndX=-4.27406 EndY=5.26292 EndZ=0
    g3: LineSegment StartX=-4.27406 StartY=5.26292 StartZ=0 EndX=-4.11052 EndY=5.35014 EndZ=0
    g4: LineSegment StartX=-4.11052 StartY=5.35014 StartZ=0 EndX=-3.97423 EndY=5.37195 EndZ=0
    g5: LineSegment StartX=-3.97423 StartY=5.37195 StartZ=0 EndX=-3.85976 EndY=5.33924 EndZ=0
    g6: LineSegment StartX=-3.85976 StartY=5.33924 StartZ=0 EndX=-3.72892 EndY=5.22476 EndZ=0
    g7: LineSegment StartX=-3.72892 StartY=5.22476 StartZ=0 EndX=-3.70712 EndY=5.12119 EndZ=0
    g8: LineSegment StartX=-3.70712 StartY=5.12119 StartZ=0 EndX=-3.75073 EndY=5.02851 EndZ=0
    g9: LineSegment StartX=-3.75073 StartY=5.02851 StartZ=0 EndX=-3.88156 EndY=4.94674 EndZ=0
    g10: LineSegment StartX=-3.88156 StartY=4.94674 StartZ=0 EndX=-4.0233 EndY=4.93039 EndZ=0
    g11: LineSegment StartX=-4.0233 StartY=4.93039 StartZ=0 EndX=-4.11597 EndY=4.95765 EndZ=0
    g12: LineSegment StartX=-4.11597 StartY=4.95765 StartZ=0 EndX=-4.23045 EndY=4.93584 EndZ=0
    g13: LineSegment StartX=-4.23045 StartY=4.93584 StartZ=0 EndX=-4.34492 EndY=4.84317 EndZ=0
    g14: LineSegment StartX=-4.34492 StartY=4.84317 StartZ=0 EndX=-4.45395 EndY=4.72869 EndZ=0
    g15: LineSegment StartX=-4.45395 StartY=4.72869 StartZ=0 EndX=-4.53572 EndY=4.58696 EndZ=0
    g16: LineSegment StartX=-4.53572 StartY=4.58696 StartZ=0 EndX=-4.56298 EndY=4.46703 EndZ=0
    g17: LineSegment StartX=-4.56298 StartY=4.46703 StartZ=0 EndX=-4.54117 EndY=4.35255 EndZ=0
    g18: LineSegment StartX=-4.54117 StartY=4.35255 StartZ=0 EndX=-4.2702 EndY=3.93667 EndZ=0
    g19: LineSegment StartX=-4.2702 StartY=3.93667 StartZ=0 EndX=-3.31154 EndY=2.85309 EndZ=0
    g20: LineSegment StartX=-3.31154 StartY=2.85309 StartZ=0 EndX=-3.27866 EndY=2.87866 EndZ=0
    g21: LineSegment StartX=-3.27866 StartY=2.87866 StartZ=0 EndX=-2.31031 EndY=1.87743 EndZ=0
    g22: LineSegment StartX=-2.31031 StartY=1.87743 StartZ=0 EndX=-2.23357 EndY=1.82262 EndZ=0
    g23: LineSegment StartX=-2.23357 StartY=1.82262 StartZ=0 EndX=-2.13856 EndY=1.77146 EndZ=0
    g24: LineSegment StartX=-2.13856 StartY=1.77146 StartZ=0 EndX=-2.03625 EndY=1.72395 EndZ=0
    g25: LineSegment StartX=-2.03625 StartY=1.72395 StartZ=0 EndX=-1.84988 EndY=1.6801 EndZ=0
    g26: LineSegment StartX=-1.84988 StartY=1.6801 StartZ=0 EndX=-1.69641 EndY=1.69837 EndZ=0
    g27: LineSegment StartX=-1.69641 StartY=1.69837 StartZ=0 EndX=-1.53563 EndY=1.73492 EndZ=0
    g28: LineSegment StartX=-1.53563 StartY=1.73492 StartZ=0 EndX=-1.426 EndY=1.808 EndZ=0
    g29: LineSegment StartX=-1.426 StartY=1.808 StartZ=0 EndX=-1.34927 EndY=1.92859 EndZ=0
    g30: LineSegment StartX=-1.34927 StartY=1.92859 StartZ=0 EndX=-1.30542 EndY=2.01994 EndZ=0
    g31: LineSegment StartX=-1.30542 StartY=2.01994 StartZ=0 EndX=-1.2908 EndY=2.16245 EndZ=0
    g32: LineSegment StartX=-1.2908 StartY=2.16245 StartZ=0 EndX=-1.32519 EndY=3.53625 EndZ=0
    g33: LineSegment StartX=-1.32519 StartY=3.53625 StartZ=0 EndX=-1.23919 EndY=3.5456 EndZ=0
    g34: LineSegment StartX=-1.23919 StartY=3.5456 StartZ=0 EndX=-1.34959 EndY=4.47961 EndZ=0
    g35: LineSegment StartX=-1.34959 StartY=4.47961 StartZ=0 EndX=-1.40651 EndY=4.82117 EndZ=0
    g36: LineSegment StartX=-1.40651 StartY=4.82117 StartZ=0 EndX=-1.49597 EndY=5.14647 EndZ=0
    g37: LineSegment StartX=-1.49597 StartY=5.14647 StartZ=0 EndX=-1.65862 EndY=5.54496 EndZ=0
    g38: LineSegment StartX=-1.65862 StartY=5.54496 StartZ=0 EndX=-1.78061 EndY=5.74014 EndZ=0
    g39: LineSegment StartX=-1.78061 StartY=5.74014 StartZ=0 EndX=-1.86193 EndY=5.78894 EndZ=0
    g40: LineSegment StartX=-1.86193 StartY=5.78894 StartZ=0 EndX=-1.98392 EndY=5.82146 EndZ=0
    g41: LineSegment StartX=-1.98392 StartY=5.82146 StartZ=0 EndX=-2.12217 EndY=5.81333 EndZ=0
    g42: LineSegment StartX=-2.12217 StartY=5.81333 StartZ=0 EndX=-2.34174 EndY=5.7564 EndZ=0
    g43: LineSegment StartX=-2.34174 StartY=5.7564 StartZ=0 EndX=-2.43933 EndY=5.71574 EndZ=0
    g44: LineSegment StartX=-2.43933 StartY=5.71574 StartZ=0 EndX=-2.4556 EndY=5.61815 EndZ=0
    g45: LineSegment StartX=-2.4556 StartY=5.61815 StartZ=0 EndX=-2.53693 EndY=5.55309 EndZ=0
    g46: LineSegment StartX=-2.53693 StartY=5.55309 StartZ=0 EndX=-2.63451 EndY=5.5287 EndZ=0
    g47: LineSegment StartX=-2.63451 StartY=5.5287 StartZ=0 EndX=-2.7809 EndY=5.54496 EndZ=0
    g48: LineSegment StartX=-2.7809 StartY=5.54496 StartZ=0 EndX=-2.81343 EndY=5.61815 EndZ=0
    g49: LineSegment StartX=-2.81343 StartY=5.61815 StartZ=0 EndX=-2.85409 EndY=5.70761 EndZ=0
    g50: LineSegment StartX=-2.85409 StartY=5.70761 StartZ=0 EndX=-2.81343 EndY=5.8052 EndZ=0
    g51: LineSegment StartX=-2.81343 StartY=5.8052 StartZ=0 EndX=-2.71584 EndY=5.93532 EndZ=0
    g52: LineSegment StartX=-2.71584 StartY=5.93532 StartZ=0 EndX=-2.60198 EndY=5.99225 EndZ=0
    g53: LineSegment StartX=-2.60198 StartY=5.99225 StartZ=0 EndX=-2.39054 EndY=6.01664 EndZ=0
    g54: LineSegment StartX=-2.39054 StartY=6.01664 StartZ=0 EndX=-2.09777 EndY=6.03291 EndZ=0
    g55: LineSegment StartX=-2.09777 StartY=6.03291 StartZ=0 EndX=-1.82127 EndY=5.98411 EndZ=0
    g56: LineSegment StartX=-1.82127 StartY=5.98411 StartZ=0 EndX=-1.62609 EndY=5.87026 EndZ=0
    g57: LineSegment StartX=-1.62609 StartY=5.87026 StartZ=0 EndX=-1.47971 EndY=5.61815 EndZ=0
    g58: LineSegment StartX=-1.47971 StartY=5.61815 StartZ=0 EndX=-1.21134 EndY=4.9025 EndZ=0
    g59: LineSegment StartX=-1.21134 StartY=4.9025 StartZ=0 EndX=-1.14627 EndY=4.54467 EndZ=0
    g60: LineSegment StartX=-1.14627 StartY=4.54467 StartZ=0 EndX=-1.04055 EndY=3.56064 EndZ=0
    g61: LineSegment StartX=-1.04055 StartY=3.56064 StartZ=0 EndX=-0.971905 EndY=3.55608 EndZ=0
    g62: LineSegment StartX=-0.971905 StartY=3.55608 StartZ=0 EndX=-0.959229 EndY=2.22692 EndZ=0
    g63: LineSegment StartX=-0.959229 StartY=2.22692 StartZ=0 EndX=-1.01922 EndY=1.91825 EndZ=0
    g64: LineSegment StartX=-1.01922 StartY=1.91825 StartZ=0 EndX=-1.12416 EndY=1.68211 EndZ=0
    g65: LineSegment StartX=-1.12416 StartY=1.68211 StartZ=0 EndX=-1.27226 EndY=1.52849 EndZ=0
    g66: LineSegment StartX=-1.27226 StartY=1.52849 StartZ=0 EndX=-0.983626 EndY=1.30795 EndZ=0
    g67: LineSegment StartX=-0.983626 StartY=1.30795 StartZ=0 EndX=-0.536341 EndY=1.06398 EndZ=0
    g68: LineSegment StartX=-0.536341 StartY=1.06398 StartZ=0 EndX=-0.145983 EndY=0.93386 EndZ=0
    g69: LineSegment StartX=-0.145983 StartY=0.93386 StartZ=0 EndX=0.179315 EndY=0.876933 EndZ=0
    g70: LineSegment StartX=0.179315 StartY=0.876933 StartZ=0 EndX=0.455818 EndY=0.909463 EndZ=0
    g71: LineSegment StartX=0.455818 StartY=0.909463 StartZ=0 EndX=0.740454 EndY=0.96639 EndZ=0
    g72: LineSegment StartX=0.740454 StartY=0.96639 StartZ=0 EndX=1.13081 EndY=1.05585 EndZ=0
    g73: LineSegment StartX=1.13081 StartY=1.05585 StartZ=0 EndX=0.821779 EndY=1.29169 EndZ=0
    g74: LineSegment StartX=0.821779 StartY=1.29169 StartZ=0 EndX=0.6266 EndY=1.52753 EndZ=0
    g75: LineSegment StartX=0.6266 StartY=1.52753 StartZ=0 EndX=0.423289 EndY=1.91789 EndZ=0
    g76: LineSegment StartX=0.423289 StartY=1.91789 StartZ=0 EndX=0.231202 EndY=2.46997 EndZ=0
    g77: LineSegment StartX=0.231202 StartY=2.46997 StartZ=0 EndX=0.215329 EndY=2.90107 EndZ=0
    g78: LineSegment StartX=0.215329 StartY=2.90107 StartZ=0 EndX=0.286801 EndY=3.262 EndZ=0
    g79: LineSegment StartX=0.286801 StartY=3.262 StartZ=0 EndX=0.463951 EndY=3.64197 EndZ=0
    g80: LineSegment StartX=0.463951 StartY=3.64197 StartZ=0 EndX=0.756719 EndY=3.91847 EndZ=0
    g81: LineSegment StartX=0.756719 StartY=3.91847 StartZ=0 EndX=1.13894 EndY=4.04859 EndZ=0
    g82: LineSegment StartX=1.13894 StartY=4.04859 StartZ=0 EndX=1.58623 EndY=4.05672 EndZ=0
    g83: LineSegment StartX=1.58623 StartY=4.05672 StartZ=0 EndX=2.00912 EndY=3.95913 EndZ=0
    g84: LineSegment StartX=2.00912 StartY=3.95913 StartZ=0 EndX=2.18888 EndY=3.81416 EndZ=0
    g85: LineSegment StartX=2.18888 StartY=3.81416 StartZ=0 EndX=2.30273 EndY=3.61898 EndZ=0
    g86: LineSegment StartX=2.30273 StartY=3.61898 StartZ=0 EndX=2.42472 EndY=3.22863 EndZ=0
    g87: LineSegment StartX=2.42472 StartY=3.22863 StartZ=0 EndX=2.44911 EndY=2.74068 EndZ=0
    g88: LineSegment StartX=2.44911 StartY=2.74068 StartZ=0 EndX=2.37592 EndY=2.2202 EndZ=0
    g89: LineSegment StartX=2.37592 StartY=2.2202 StartZ=0 EndX=2.18074 EndY=1.71599 EndZ=0
    g90: LineSegment StartX=2.18074 StartY=1.71599 StartZ=0 EndX=1.9449 EndY=1.41509 EndZ=0
    g91: LineSegment StartX=1.9449 StartY=1.41509 StartZ=0 EndX=1.71719 EndY=1.15485 EndZ=0
    g92: LineSegment StartX=1.71719 StartY=1.15485 StartZ=0 EndX=1.58707 EndY=1.05726 EndZ=0
    g93: LineSegment StartX=1.58707 StartY=1.05726 StartZ=0 EndX=1.89611 EndY=0.935272 EndZ=0
    g94: LineSegment StartX=1.89611 StartY=0.935272 StartZ=0 EndX=2.2946 EndY=0.837682 EndZ=0
    g95: LineSegment StartX=2.2946 StartY=0.837682 StartZ=0 EndX=2.80566 EndY=0.722268 EndZ=0
    g96: LineSegment StartX=2.80566 StartY=0.722268 StartZ=0 EndX=3.33522 EndY=0.650048 EndZ=0
    g97: LineSegment StartX=3.33522 StartY=0.650048 StartZ=0 EndX=3.33555 EndY=0.618106 EndZ=0
    g98: LineSegment StartX=3.33555 StartY=0.618106 StartZ=0 EndX=3.67187 EndY=0.588286 EndZ=0
    g99: LineSegment StartX=-4.74287 StartY=4.61966 StartZ=0 EndX=-4.77857 EndY=4.46074 EndZ=0
    g100: LineSegment StartX=-4.77857 StartY=4.46074 StartZ=0 EndX=-4.70537 EndY=4.24116 EndZ=0
    g101: LineSegment StartX=-4.70537 StartY=4.24116 StartZ=0 EndX=-4.4858 EndY=3.91586 EndZ=0
    g102: LineSegment StartX=-4.4858 StartY=3.91586 StartZ=0 EndX=-4.15237 EndY=3.49297 EndZ=0
    g103: LineSegment StartX=-4.15237 StartY=3.49297 StartZ=0 EndX=-3.43671 EndY=2.70412 EndZ=0
    g104: LineSegment StartX=-3.43671 StartY=2.70412 StartZ=0 EndX=-3.47737 EndY=2.66346 EndZ=0
    g105: LineSegment StartX=-3.47737 StartY=2.66346 StartZ=0 EndX=-2.43642 EndY=1.63064 EndZ=0
    g106: LineSegment StartX=-2.43642 StartY=1.63064 StartZ=0 EndX=-2.21684 EndY=1.49239 EndZ=0
    g107: LineSegment StartX=-2.21684 StartY=1.49239 StartZ=0 EndX=-1.85088 EndY=1.3948 EndZ=0
    g108: LineSegment StartX=-1.85088 StartY=1.3948 StartZ=0 EndX=-1.51745 EndY=1.40293 EndZ=0
    g109: LineSegment StartX=-1.51745 StartY=1.40293 StartZ=0 EndX=-1.431 EndY=1.42436 EndZ=0
    g110: LineSegment StartX=-1.431 StartY=1.42436 StartZ=0 EndX=-0.915646 EndY=1.0207 EndZ=0
    g111: LineSegment StartX=-0.915646 StartY=1.0207 StartZ=0 EndX=-0.679804 EndY=0.923115 EndZ=0
    g112: LineSegment StartX=-0.679804 StartY=0.923115 StartZ=0 EndX=-0.354506 EndY=0.80926 EndZ=0
    g113: LineSegment StartX=-0.354506 StartY=0.80926 StartZ=0 EndX=-0.029207 EndY=0.719803 EndZ=0
    g114: LineSegment StartX=-0.029207 StartY=0.719803 StartZ=0 EndX=0.401813 EndY=0.703538 EndZ=0
    g115: LineSegment StartX=0.401813 StartY=0.703538 StartZ=0 EndX=0.840967 EndY=0.768598 EndZ=0
    g116: LineSegment StartX=0.840967 StartY=0.768598 StartZ=0 EndX=1.18253 EndY=0.866187 EndZ=0
    g117: LineSegment StartX=1.18253 StartY=0.866187 StartZ=0 EndX=1.35925 EndY=0.932894 EndZ=0
    g118: LineSegment StartX=1.35925 StartY=0.932894 StartZ=0 EndX=1.92422 EndY=0.73671 EndZ=0
    g119: LineSegment StartX=1.92422 StartY=0.73671 StartZ=0 EndX=2.42589 EndY=0.614738 EndZ=0
    g120: LineSegment StartX=2.42589 StartY=0.614738 StartZ=0 EndX=2.78568 EndY=0.537491 EndZ=0
    g121: LineSegment StartX=2.78568 StartY=0.537491 StartZ=0 EndX=3.32194 EndY=0.464846 EndZ=0
    g122: LineSegment StartX=3.32194 StartY=0.464846 StartZ=0 EndX=3.32187 EndY=0.504415 EndZ=0
    g123: LineSegment StartX=3.32187 StartY=0.504415 StartZ=0 EndX=3.66987 EndY=0.473498 EndZ=0
    g124: ArcOfCircle CenterX=4.51096 CenterY=0.516202 CenterZ=0 NormalX=0 NormalY=0 NormalZ=1 AngleXU=0 Radius=0.842176 StartAngle=3.19232 EndAngle=9.33908
    g125: LineSegment StartX=1.34342 StartY=1.14005 StartZ=0 EndX=1.11529 EndY=1.30538 EndZ=0
    g126: LineSegment StartX=1.11529 StartY=1.30538 StartZ=0 EndX=0.838842 EndY=1.60821 EndZ=0
    g127: LineSegment StartX=0.838842 StartY=1.60821 StartZ=0 EndX=0.666136 EndY=1.93283 EndZ=0
    g128: LineSegment StartX=0.666136 StartY=1.93283 StartZ=0 EndX=0.553143 EndY=2.20786 EndZ=0
    g129: LineSegment StartX=0.553143 StartY=2.20786 StartZ=0 EndX=0.454383 EndY=2.5027 EndZ=0
    g130: LineSegment StartX=0.454383 StartY=2.5027 StartZ=0 EndX=0.425845 EndY=2.85118 EndZ=0
    g131: LineSegment StartX=0.425845 StartY=2.85118 StartZ=0 EndX=0.493159 EndY=3.18633 EndZ=0
    g132: LineSegment StartX=0.493159 StartY=3.18633 StartZ=0 EndX=0.598829 EndY=3.49351 EndZ=0
    g133: LineSegment StartX=0.598829 StartY=3.49351 StartZ=0 EndX=0.856165 EndY=3.73528 EndZ=0
    g134: LineSegment StartX=0.856165 StartY=3.73528 StartZ=0 EndX=1.0797 EndY=3.84629 EndZ=0
    g135: LineSegment StartX=1.0797 StartY=3.84629 StartZ=0 EndX=1.36866 EndY=3.87522 EndZ=0
    g136: LineSegment StartX=1.36866 StartY=3.87522 StartZ=0 EndX=1.69738 EndY=3.82301 EndZ=0
    g137: LineSegment StartX=1.69738 StartY=3.82301 StartZ=0 EndX=1.95995 EndY=3.70829 EndZ=0
    g138: LineSegment StartX=1.95995 StartY=3.70829 StartZ=0 EndX=2.1123 EndY=3.49431 EndZ=0
    g139: LineSegment StartX=2.1123 StartY=3.49431 StartZ=0 EndX=2.20217 EndY=3.2215 EndZ=0
    g140: LineSegment StartX=2.20217 StartY=3.2215 StartZ=0 EndX=2.23673 EndY=2.86405 EndZ=0
    g141: LineSegment StartX=2.23673 StartY=2.86405 StartZ=0 EndX=2.21642 EndY=2.49934 EndZ=0
    g142: LineSegment StartX=2.21642 StartY=2.49934 StartZ=0 EndX=2.08949 EndY=2.02799 EndZ=0
    g143: LineSegment StartX=2.08949 StartY=2.02799 StartZ=0 EndX=1.90818 EndY=1.68312 EndZ=0
    g144: LineSegment StartX=1.90818 StartY=1.68312 StartZ=0 EndX=1.68974 EndY=1.40949 EndZ=0
    g145: LineSegment StartX=1.68974 StartY=1.40949 StartZ=0 EndX=1.48022 EndY=1.22224 EndZ=0
    g146: LineSegment StartX=1.48022 StartY=1.22224 StartZ=0 EndX=1.34342 EndY=1.14005 EndZ=0
  constraints (145):
    c: Coincident(g0,g1)
    c: Coincident(g1,g2)
    c: Coincident(g2,g3)
    c: Coincident(g3,g4)
    c: Coincident(g4,g5)
    c: Coincident(g5,g6)
    c: Coincident(g6,g7)
    c: Coincident(g7,g8)
    c: Coincident(g8,g9)
    c: Coincident(g9,g10)
    c: Coincident(g10,g11)
    c: Coincident(g11,g12)
    c: Coincident(g12,g13)
    c: Coincident(g13,g14)
    c: Coincident(g14,g15)
    c: Coincident(g15,g16)
    c: Coincident(g16,g17)
    c: Coincident(g18,g19)
    c: Coincident(g19,g20)
    c: Coincident(g20,g21)
    c: Coincident(g21,g22)
    c: Coincident(g22,g23)
    c: Coincident(g23,g24)
    c: Coincident(g24,g25)
    c: Coincident(g25,g26)
    c: Coincident(g26,g27)
    c: Coincident(g27,g28)
    c: Coincident(g28,g29)
    c: Coincident(g29,g30)
    c: Coincident(g30,g31)
    c: Coincident(g31,g32)
    c: Coincident(g32,g33)
    c: Coincident(g33,g34)
    c: Coincident(g34,g35)
    c: Coincident(g35,g36)
    c: Coincident(g36,g37)
    c: Coincident(g37,g38)
    c: Coincident(g38,g39)
    c: Coincident(g39,g40)
    c: Coincident(g40,g41)
    c: Coincident(g41,g42)
    c: Coincident(g42,g43)
    c: Coincident(g43,g44)
    c: Coincident(g44,g45)
    c: Coincident(g45,g46)
    c: Coincident(g46,g47)
    c: Coincident(g47,g48)
    c: Coincident(g48,g49)
    c: Coincident(g49,g50)
    c: Coincident(g50,g51)
    c: Coincident(g51,g52)
    c: Coincident(g52,g53)
    c: Coincident(g53,g54)
    c: Coincident(g54,g55)
    c: Coincident(g55,g56)
    c: Coincident(g56,g57)
    c: Coincident(g57,g58)
    c: Coincident(g58,g59)
    c: Coincident(g59,g60)
    c: Coincident(g60,g61)
    c: Coincident(g61,g62)
    c: Coincident(g62,g63)
    c: Coincident(g63,g64)
    c: Coincident(g64,g65)
    c: Coincident(g65,g66)
    c: Coincident(g66,g67)
    c: Coincident(g67,g68)
    c: Coincident(g68,g69)
    c: Coincident(g69,g70)
    c: Coincident(g70,g71)
    c: Coincident(g71,g72)
    c: Coincident(g72,g73)
    c: Coincident(g73,g74)
    c: Coincident(g74,g75)
    c: Coincident(g75,g76)
    c: Coincident(g76,g77)
    c: Coincident(g77,g78)
    c: Coincident(g78,g79)
    c: Coincident(g79,g80)
    c: Coincident(g80,g81)
    c: Coincident(g81,g82)
    c: Coincident(g82,g83)
    c: Coincident(g83,g84)
    c: Coincident(g84,g85)
    c: Coincident(g85,g86)
    c: Coincident(g86,g87)
    c: Coincident(g87,g88)
    c: Coincident(g88,g89)
    c: Coincident(g89,g90)
    c: Coincident(g90,g91)
    c: Coincident(g91,g92)
    c: Coincident(g92,g93)
    c: Coincident(g93,g94)
    c: Coincident(g94,g95)
    c: Coincident(g95,g96)
    c: Coincident(g96,g97)
    c: Coincident(g97,g98)
    c: Coincident(g99,g100)
    c: Coincident(g100,g101)
    c: Coincident(g101,g102)
    c: Coincident(g102,g103)
    c: Coincident(g103,g104)
    c: Coincident(g104,g105)
    c: Coincident(g105,g106)
    c: Coincident(g106,g107)
    c: Coincident(g107,g108)
    c: Coincident(g108,g109)
    c: Coincident(g109,g110)
    c: Coincident(g110,g111)
    c: Coincident(g111,g112)
    c: Coincident(g112,g113)
    c: Coincident(g113,g114)
    c: Coincident(g114,g115)
    c: Coincident(g115,g116)
    c: Coincident(g116,g117)
    c: Coincident(g117,g118)
    c: Coincident(g118,g119)
    c: Coincident(g119,g120)
    c: Coincident(g120,g121)
    c: Coincident(g121,g122)
    c: Coincident(g122,g123)
    c: Coincident(g123,g124)
    c: Coincident(g125,g126)
    c: Coincident(g126,g127)
    c: Coincident(g127,g128)
    c: Coincident(g128,g129)
    c: Coincident(g129,g130)
    c: Coincident(g130,g131)
    c: Coincident(g131,g132)
    c: Coincident(g132,g133)
    c: Coincident(g133,g134)
    c: Coincident(g134,g135)
    c: Coincident(g135,g136)
    c: Coincident(g136,g137)
    c: Coincident(g137,g138)
    c: Coincident(g138,g139)
    c: Coincident(g139,g140)
    c: Coincident(g140,g141)
    c: Coincident(g141,g142)
    c: Coincident(g142,g143)
    c: Coincident(g143,g144)
    c: Coincident(g144,g145)
    c: Coincident(g145,g146)
    c: Coincident(g146,g125)
    c: Coincident(g124,g98)
FEATURE [PartDesign::Body] Body003
  Group = -> [Sketch003]
  Origin = -> Origin003
FEATURE [Part::Extrusion] Extrude003
  Base = -> Sketch003
  Dir = (0,0,1)
  DirMode = 2
  FaceMakerClass = Part::FaceMakerBullseye
  LengthFwd = 1
  LengthRev = 0
  Placement = pos=(2,19,0) rot=(0,0,1;0.523599rad)
  Solid = true
  Symmetric = false
FEATURE [Part::Cut] Cut
  Base = -> Extrude002
  Placement = pos=(0,0,1) rot=(0,0,1;0rad)
  Tool = -> Extrude003
FEATURE [Part::Cylinder] Cylinder  label="Okvir"
  Angle = 360
  AttacherType = Attacher::AttachEngine3D
  Height = 2.2
  Placement = pos=(30,20,0) rot=(0,0,1;0rad)
  Radius = 14
FEATURE [Part::Cylinder] Cylinder001  label="izrez"
  Angle = 360
  AttacherType = Attacher::AttachEngine3D
  Height = 3
  Placement = pos=(30,20,1) rot=(0,0,1;0rad)
  Radius = 13
FEATURE [Part::Cut] Cut001
  Base = -> Cylinder
  Tool = -> Cylinder001
FEATURE [Part::Part2DObjectPython] ShapeString  # Draft 2D object (typed FeaturePython)
  FontFile = <path>
  Placement = pos=(20.22,25.62,1) rot=(0,0,1;0.017453rad)
  Size = 3.5
  String = Porodični
  Tracking = 0
FEATURE [Part::Extrusion] Extrude004
  Base = -> ShapeString
  Dir = (0,0,1)
  DirMode = 2
  FaceMakerClass = Part::FaceMakerBullseye
  LengthFwd = 3
  LengthRev = 0
  Placement = pos=(62,-3,1.5) rot=(0,1,0;3.14159rad)
  Solid = true
  Symmetric = false
FEATURE [Part::Part2DObjectPython] ShapeString001  # Draft 2D object (typed FeaturePython)
  FontFile = <path>
  Placement = pos=(30,20,1) rot=(0,0,1;0rad)
  Size = 3.5
  String = Lekar
  Tracking = 0
FEATURE [Part::Extrusion] Extrude005
  Base = -> ShapeString001
  Dir = (0,0,1)
  DirMode = 2
  FaceMakerClass = Part::FaceMakerBullseye
  LengthFwd = 3
  LengthRev = 0
  Placement = pos=(66,-2.5,1.5) rot=(0,1,0;3.14159rad)
  Solid = true
  Symmetric = false
FEATURE [Part::Part2DObjectPython] ShapeString002  # Draft 2D object (typed FeaturePython)
  FontFile = <path>
  Placement = pos=(22,10,1) rot=(0,0,1;0rad)
  Size = 3.5
  String = Slavica
  Tracking = 0
FEATURE [Part::Extrusion] Extrude001
  Base = -> Sketch001
  Dir = (0,0,1)
  DirMode = 2
  FaceMakerClass = Part::FaceMakerBullseye
  LengthFwd = 1
  LengthRev = 0
  Placement = pos=(1.5,19.7,2) rot=(0,1,0;3.14159rad)
  Solid = true
  Symmetric = false
FEATURE [Part::Cut] Cut003
  Base = -> Cut001
  Tool = -> Extrude004
FEATURE [Part::Cut] Cut004
  Base = -> Cut003
  Tool = -> Extrude005
FEATURE [Part::Extrusion] Extrude006
  Base = -> ShapeString002
  Dir = (0,0,1)
  DirMode = 2
  FaceMakerClass = Part::FaceMakerBullseye
  LengthFwd = 3
  LengthRev = 0
  Placement = pos=(60,2,1.5) rot=(0,1,0;3.14159rad)
  Solid = false
  Symmetric = false
FEATURE [Part::Cut] Cut005
  Base = -> Cut004
  Placement = pos=(-29,0,0) rot=(0,0,1;0rad)
  Tool = -> Extrude006
FEATURE [Part::Cylinder] Cylinder002  label="Cylinder"
  Angle = 360
  AttacherType = Attacher::AttachEngine3D
  Height = 2
  Placement = pos=(0,36,0) rot=(0,0,1;0rad)
  Radius = 3
FEATURE [Part::Box] Box  label="Cube"
  AttacherType = Attacher::AttachEngine3D
  Height = 2
  Length = 6
  Placement = pos=(-3,33,0) rot=(0,0,1;0rad)
  Width = 3
FEATURE [Part::Cylinder] Cylinder003  label="Cylinder001"
  Angle = 360
  AttacherType = Attacher::AttachEngine3D
  Height = 10
  Placement = pos=(0,36,0) rot=(0,0,1;0rad)
  Radius = 1.5
FEATURE [Part::Cut] Cut006
  Base = -> Cylinder002
  Tool = -> Cylinder003
FEATURE [Part::Cut] Cut007
  Base = -> Box
  Tool = -> Cylinder003
note: 3 file-system paths scrubbed to <path> (originals preserved in the JSON sidecar)
